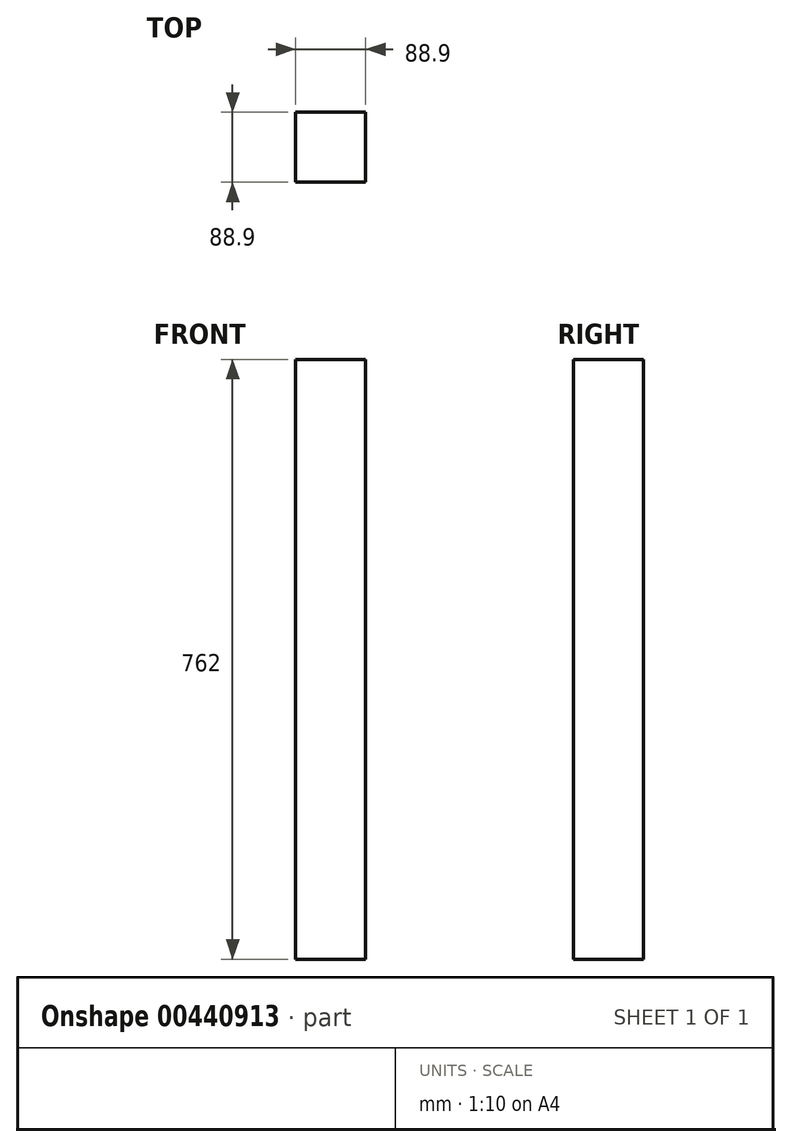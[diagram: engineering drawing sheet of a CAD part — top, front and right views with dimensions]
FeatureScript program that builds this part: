
annotation { "Feature Type Name" : "Feature", "Feature Type Description" : "" }
export const myFeature = defineFeature(function(context is Context, id is Id, definition is map)
    precondition{}
    {
        {
            var Q0;
            Q0=qCreatedBy(makeId("Top.planeOp"),FACE);
            var sketch = newSketch(context, id + "F0", { "sketchPlane" : qUnion([Q0])});
            skLineSegment(sketch, "E0.bottom", {"start": v(44.45, 44.45) * mm, "end": v(-44.45, 44.45) * mm});
            skLineSegment(sketch, "E0.top", {"start": v(44.45, -44.45) * mm, "end": v(-44.45, -44.45) * mm});
            skLineSegment(sketch, "E0.left", {"start": v(44.45, 44.45) * mm, "end": v(44.45, -44.45) * mm});
            skLineSegment(sketch, "E0.right", {"start": v(-44.45, 44.45) * mm, "end": v(-44.45, -44.45) * mm});
            skPoint(sketch, "E0.middle", {"position": v(0, 0) * mm});
            skSolve(sketch);
        }
        {
            var Q0;
            Q0 = qSketchRegion(id + "F0", true);
            extrude(context, id + "F1", {"entities" : qUnion([Q0]), "depth" : 762 * mm});
        }
    });
